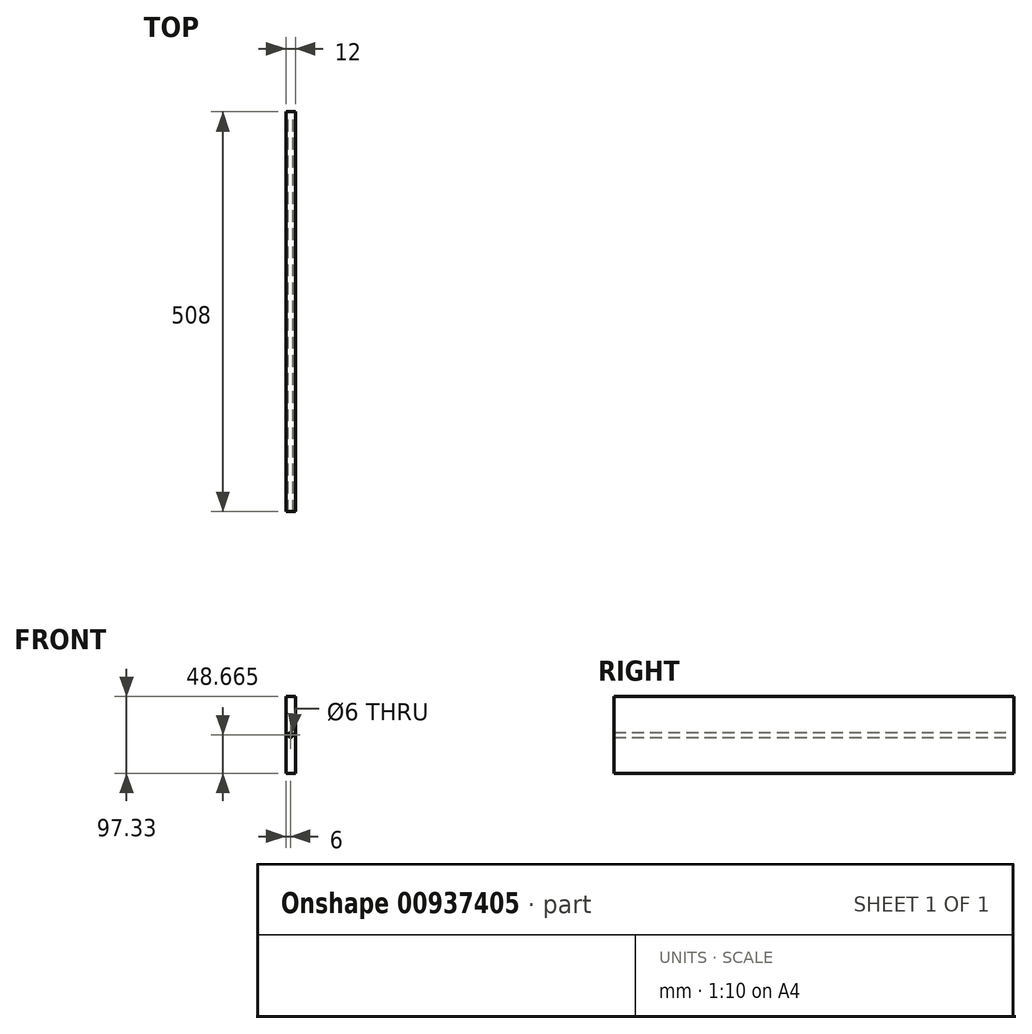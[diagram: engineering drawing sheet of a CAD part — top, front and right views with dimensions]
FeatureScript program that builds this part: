
annotation { "Feature Type Name" : "Feature", "Feature Type Description" : "" }
export const myFeature = defineFeature(function(context is Context, id is Id, definition is map)
    precondition{}
    {
        {
            var Q0;
            Q0=qCreatedBy(makeId("Front.planeOp"),FACE);
            var sketch = newSketch(context, id + "F0", { "sketchPlane" : qUnion([Q0])});
            skLineSegment(sketch, "E0.bottom", {"start": v(0, 0) * mm, "end": v(12, 0) * mm});
            skLineSegment(sketch, "E0.top", {"start": v(0, -97.33) * mm, "end": v(12, -97.33) * mm});
            skLineSegment(sketch, "E0.left", {"start": v(0, 0) * mm, "end": v(0, -97.33) * mm});
            skLineSegment(sketch, "E0.right", {"start": v(12, 0) * mm, "end": v(12, -97.33) * mm});
            skCircle(sketch, "E1", {"center": v(6, -48.66) * mm, "radius": 3 * mm});
            skPoint(sketch, "E2.orphan", {"position": v(0, -48.66) * mm});
            skPoint(sketch, "E3.end.orphan", {"position": v(12, -48.66) * mm});
            skSolve(sketch);
        }
        {
            var Q0;
            Q0 = qSketchRegion(id + "F0", true);
            extrude(context, id + "F1", {"entities" : qUnion([Q0]), "depth" : 508 * mm, "offsetDistance" : 25 * mm});
        }
    });
